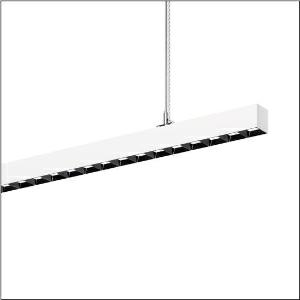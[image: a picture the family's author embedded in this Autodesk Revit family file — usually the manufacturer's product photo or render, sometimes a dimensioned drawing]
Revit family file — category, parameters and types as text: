
# Revit family: silica_r__21_51mx31dc3dwb_5f0e
name_source: partatom
category: Lighting Fixtures
units: mm (PartAtom-declared; Revit-internal decimal feet)

## family parameters
Cut with Voids When Loaded = No
Host = Face
Light Source = No
Part Type = Normal
Room Calculation Point = No
Round Connector Dimension = Use Diameter
Shared = No

## types (1)
- --- (1 x LED, 18230 lm, 113.3 W, 3000K)
    Apparent Load = 113 VA
    CIE Flux Codes = 87 99 100 59 100
    Color Rendering = 80
    Color Temperature = 3000K
    Default Elevation = 1800 mm
    Description = Silica® 21, office luminaire, primary light control with darklight reflector, of PMMA, black, CAT 2 (L<= 3000cd/m²), light emission: direct/indirect distribution, primary light characteristic: symmetric, installation type: suspended mounting, LED, rated luminous flux: 18.230lm, luminous efficacy: 161lm/W, light colour: 830, colour temperature: 3000K, with terminal, 3+2-pole, max. 2.5mm², mains connection: 220..240V, AC, 50/60Hz, rated input power: 113.3W, luminaire housing, of aluminium, traffic white (RAL 9016), length: 3.004mm, width: 53mm, height: 53mm, protection rating (complete): IP20, insulation class (complete): insulation class I (protective earthing), certification: CE, permissible operating ambient temperature: 0..+35°C, standard: EN 50419, packaging unit: 1 piece
    Height = 53 mm
    Lamp = 1 x LED
    Lamp Light Flux = 18230 lm
    Lamp Power = 113.3 W
    Lamp count = 1
    Length = 3004 mm
    Luminous efficacy = 161 lm/W
    Manufacturer = Siteco
    ModVariant = No
    Model = 51MX31DC3DWB
    Mounting Place = Ceiling
    Mounting Type = Pendant
    Number of Poles = 1
    OnlyDefault = Yes
    Power Factor = 1
    Product Name = Silica® 21
    Product group = office luminaire | ceiling pendant
    ProductGroupID = 902
    Protection Class = Protection class I
    Protection Degree = IP 20
    RLX_Detail_Level = 1
    RLX_Emergency_Light_Flux = 0 lm
    RLX_Emergency_Type = 0
    RLX_Emergency_Type_DB = No
    RlxData = <blob elided: 64709 chars, md5=947d3f64>
    Socket = socket
    Standby Power = 0 W
    System Light Flux = 18230 lm
    System Power = 113 W
    Type Comments = factory setting: luminous flux: 100 % | dim-lin: 254 | 392 mA
    Type Image = l_1335871.jpg
    URL = http://relux.com
    VarID = @adj_090689
    Voltage = 0 V
    Weight = 0.00 kg
    Width = 53 mm

## geometry (parser evidence)
native form markers: Blend x4, Sweep x12
no freeform markers — native parametric forms only
